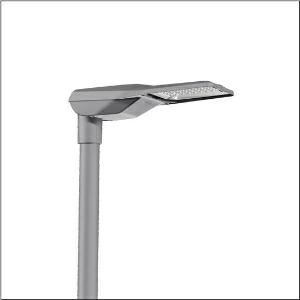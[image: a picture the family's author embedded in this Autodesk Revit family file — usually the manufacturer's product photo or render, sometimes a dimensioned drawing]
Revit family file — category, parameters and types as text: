
# Revit family: streetlight_sl_21_mini___p1_0a_5xe6a33a08hb_d31a
name_source: partatom
category: Lighting Fixtures
units: mm (PartAtom-declared; Revit-internal decimal feet)

## family parameters
Cut with Voids When Loaded = No
Host = Face
Light Source = No
Part Type = Normal
Room Calculation Point = No
Round Connector Dimension = Use Diameter
Shared = No

## types (1)
- --- (1 x LED, 9040 lm, 66 W, 3000K)
    Apparent Load = 66 VA
    CIE Flux Codes = 21 50 90 100 100
    Color Rendering = 70
    Color Temperature = 3000K
    Default Elevation = 1800 mm
    Description = Streetlight SL 21 mini, mast luminaire, primary light control with lens, of PMMA, primary optical cover: cover, of toughened safety glass, transparent, light distribution: P1.0a, light emission: direct distribution, primary light characteristic: asymmetric, installation type: post-top, side-entry, LED, 3G 1.5mm², High Power LED, rated luminous flux: 9.040lm, luminous efficacy: 137lm/W, light colour: 730, colour temperature: 3000K, control: overheat protection, constant luminous flux control, time-dependent luminous flux control, flexible luminous flux parameterisation, mains connection: 230..240V, AC, 50/60Hz, connection cable pre-assembled, cable length: 8,5m, wiring characteristics: H07RN-F, start of lifetime: 66W, end of service life: 69W, reduction: 30W, luminaire housing, of diecast aluminium, powder-coated, Siteco® metallic grey (DB 702S), corrosivity category C5 mid according to DIN EN ISO 12944, please order mast flange separately, inclination adjustable: 0°, 5°, 10°, 15°, sealing non-destructively replaceable, multi-level sealing system, length: 628mm, width: 235mm, height: 110mm, mast flange for spigot size: 42mm (side-entry): 5XC10008XM4, 60/48mm (side-entry/post-top): 5XC10108XM2, 76/60mm (side-entry/post-top): 5XC10108XM1, protection rating (complete): IP66, insulation class (complete): insulation class II (safety insulation), certification: CE, ENEC, ENEC+, VDE, impact resistance: IK09, permissible operating ambient temperature for outdoor applications: -40..+50°C, standard-compliant lighting for roads and squares, packaging unit: 1 piece

Light Distribution: P1.0a
    Height = 110 mm
    Lamp = 1 x LED
    Lamp Light Flux = 9040 lm
    Lamp Power = 66 W
    Lamp count = 1
    Length = 625 mm
    Luminous efficacy = 137 lm/W
    Manufacturer = Siteco
    ModVariant = No
    Model = 5XE6A33A08HB
    Number of Poles = 1
    OnlyDefault = Yes
    Power Factor = 1
    Product Name = Streetlight SL 21 mini | P1.0a
    Product group = mast luminaire | pylon top
    ProductGroupID = 6100
    Protection Class = Protection class II
    Protection Degree = IP 66
    RLX_Detail_Level = 1
    RLX_Emergency_Light_Flux = 0 lm
    RLX_Emergency_Type = 0
    RLX_Emergency_Type_DB = No
    RlxData = <blob elided: 103633 chars, md5=d24e5731>
    Socket = socket
    Standby Power = 0 W
    System Light Flux = 9040 lm
    System Power = 66 W
    Type Comments = factory setting: luminous flux: 100 % | Output Level: 100 % | 670 mA
    Type Image = l_1003519.jpg
    URL = http://relux.com
    VarID = @adj_158219
    Voltage = 0 V
    Weight = 0.00 kg
    Width = 234 mm

## geometry (parser evidence)
native form markers: Blend x4, Sweep x10
no freeform markers — native parametric forms only
